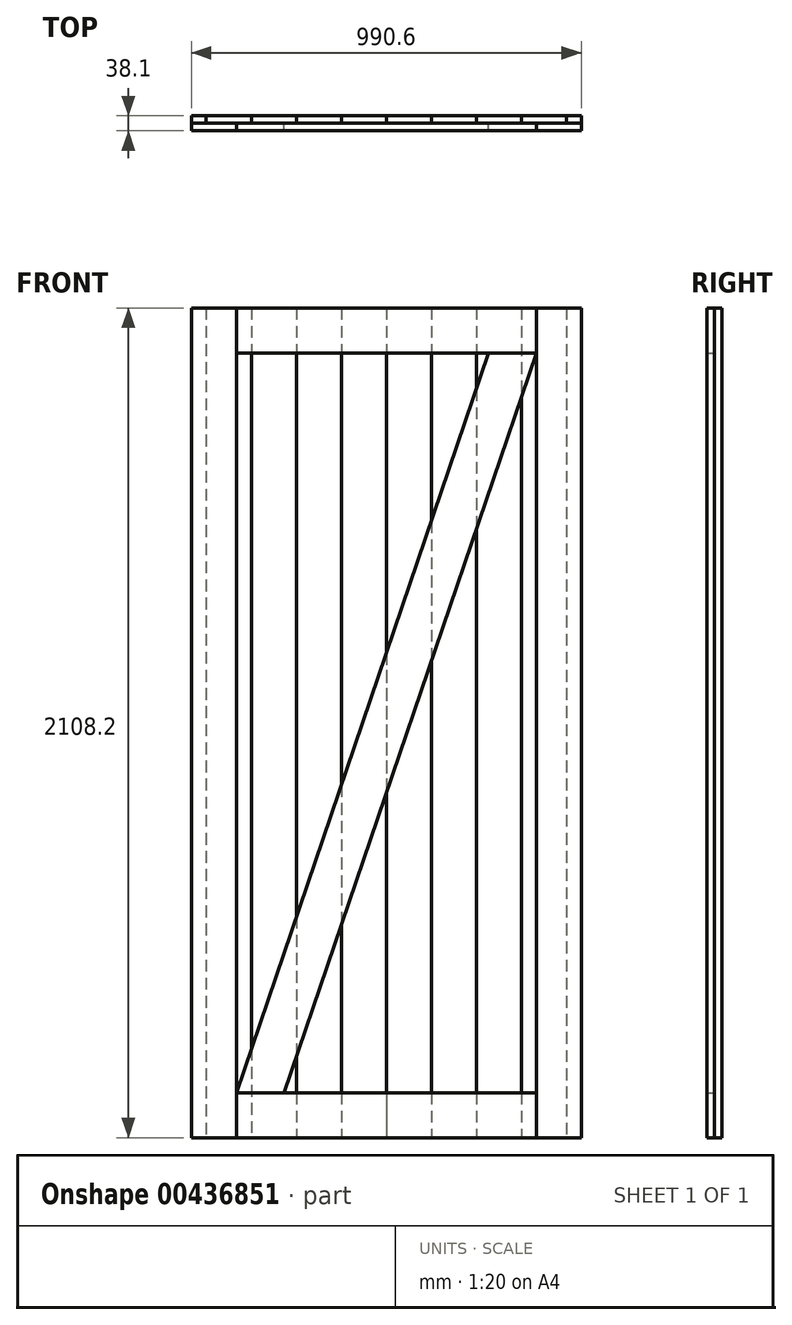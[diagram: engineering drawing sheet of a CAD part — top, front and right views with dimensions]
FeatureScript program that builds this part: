
annotation { "Feature Type Name" : "Feature", "Feature Type Description" : "" }
export const myFeature = defineFeature(function(context is Context, id is Id, definition is map)
    precondition{}
    {
        {
            var Q0;
            Q0=qCreatedBy(makeId("Top.planeOp"),FACE);
            var sketch = newSketch(context, id + "F0", { "sketchPlane" : qUnion([Q0])});
            skLineSegment(sketch, "E0.bottom", {"start": v(0, 0) * mm, "end": v(114.3, 0) * mm});
            skLineSegment(sketch, "E0.top", {"start": v(0, 19.05) * mm, "end": v(114.3, 19.05) * mm});
            skLineSegment(sketch, "E0.left", {"start": v(0, 0) * mm, "end": v(0, 19.05) * mm});
            skLineSegment(sketch, "E0.right", {"start": v(114.3, 0) * mm, "end": v(114.3, 19.05) * mm});
            skSolve(sketch);
        }
        {
            var Q0;
            Q0 = qSketchRegion(id + "F0", true);
            extrude(context, id + "F1", {"entities" : qUnion([Q0]), "depth" : 2108.2 * mm});
        }
        {
            var Q0;
            Q0=makeQuery(id+"F1.opExtrude","SWEPT_BODY",BODY,{"disambiguationData":[OSD([sQuery(id+"F0.wireOp",EDGE,"E0.bottom"),sQuery(id+"F0.wireOp",EDGE,"E0.top"),sQuery(id+"F0.wireOp",EDGE,"E0.left"),sQuery(id+"F0.wireOp",EDGE,"E0.right")])]});
            var Q1;
            Q1=makeQuery(id+"F1.opExtrude","CAP_EDGE",EDGE,{"disambiguationData":[OSD([sQuery(id+"F0.wireOp",EDGE,"E0.bottom")])],"isStart":true});
            transform(context, id + "F2", {"entities" : qUnion([Q0]), "transformType" : TransformType.TRANSLATION_ENTITY, "oppositeDirectionEntity" : false, "transformLine" : qUnion([Q1]), "makeCopy" : true});
        }
        {
            var Q0;
            Q0=makeQuery(id+"F1.opExtrude","SWEPT_BODY",BODY,{"disambiguationData":[OSD([sQuery(id+"F0.wireOp",EDGE,"E0.bottom"),sQuery(id+"F0.wireOp",EDGE,"E0.top"),sQuery(id+"F0.wireOp",EDGE,"E0.left"),sQuery(id+"F0.wireOp",EDGE,"E0.right")])]});
            var Q1;
            Q1=makeQuery(id+"F2.opPattern","COPY",BODY,{"derivedFrom":makeQuery(id+"F1.opExtrude","SWEPT_BODY",BODY,{"disambiguationData":[OSD([sQuery(id+"F0.wireOp",EDGE,"E0.bottom"),sQuery(id+"F0.wireOp",EDGE,"E0.top"),sQuery(id+"F0.wireOp",EDGE,"E0.left"),sQuery(id+"F0.wireOp",EDGE,"E0.right")])]}),"instanceName":"1"});
            var Q2;
            Q2=makeQuery(id+"F1.opExtrude","CAP_FACE",FACE,{"disambiguationData":[OSD([sQuery(id+"F0.wireOp",EDGE,"E0.bottom"),sQuery(id+"F0.wireOp",EDGE,"E0.top"),sQuery(id+"F0.wireOp",EDGE,"E0.left"),sQuery(id+"F0.wireOp",EDGE,"E0.right")])],"isStart":true});
            var Q3;
            Q3=makeQuery(id+"F2.opPattern","COPY",EDGE,{"derivedFrom":makeQuery(id+"F1.opExtrude","CAP_EDGE",EDGE,{"disambiguationData":[OSD([sQuery(id+"F0.wireOp",EDGE,"E0.bottom")])],"isStart":true}),"instanceName":"1"});
            transform(context, id + "F3", {"entities" : qUnion([Q0, Q1]), "transformType" : TransformType.TRANSLATION_DISTANCE, "transformDirection" : qUnion([Q2, Q3]), "distance" : 228.6 * mm, "makeCopy" : true});
        }
        {
            var Q0;
            Q0=makeQuery(id+"F1.opExtrude","SWEPT_BODY",BODY,{"disambiguationData":[OSD([sQuery(id+"F0.wireOp",EDGE,"E0.bottom"),sQuery(id+"F0.wireOp",EDGE,"E0.top"),sQuery(id+"F0.wireOp",EDGE,"E0.left"),sQuery(id+"F0.wireOp",EDGE,"E0.right")])]});
            var Q1;
            Q1=makeQuery(id+"F2.opPattern","COPY",BODY,{"derivedFrom":makeQuery(id+"F1.opExtrude","SWEPT_BODY",BODY,{"disambiguationData":[OSD([sQuery(id+"F0.wireOp",EDGE,"E0.bottom"),sQuery(id+"F0.wireOp",EDGE,"E0.top"),sQuery(id+"F0.wireOp",EDGE,"E0.left"),sQuery(id+"F0.wireOp",EDGE,"E0.right")])]}),"instanceName":"1"});
            var Q2;
            Q2=makeQuery(id+"F3.opPattern","COPY",BODY,{"derivedFrom":makeQuery(id+"F1.opExtrude","SWEPT_BODY",BODY,{"disambiguationData":[OSD([sQuery(id+"F0.wireOp",EDGE,"E0.bottom"),sQuery(id+"F0.wireOp",EDGE,"E0.top"),sQuery(id+"F0.wireOp",EDGE,"E0.left"),sQuery(id+"F0.wireOp",EDGE,"E0.right")])]}),"instanceName":"1"});
            var Q3;
            Q3=makeQuery(id+"F3.opPattern","COPY",BODY,{"derivedFrom":makeQuery(id+"F2.opPattern","COPY",BODY,{"derivedFrom":makeQuery(id+"F1.opExtrude","SWEPT_BODY",BODY,{"disambiguationData":[OSD([sQuery(id+"F0.wireOp",EDGE,"E0.bottom"),sQuery(id+"F0.wireOp",EDGE,"E0.top"),sQuery(id+"F0.wireOp",EDGE,"E0.left"),sQuery(id+"F0.wireOp",EDGE,"E0.right")])]}),"instanceName":"1"}),"instanceName":"1"});
            var Q4;
            Q4=makeQuery(id+"F3.opPattern","COPY",EDGE,{"derivedFrom":makeQuery(id+"F2.opPattern","COPY",EDGE,{"derivedFrom":makeQuery(id+"F1.opExtrude","CAP_EDGE",EDGE,{"disambiguationData":[OSD([sQuery(id+"F0.wireOp",EDGE,"E0.bottom")])],"isStart":true}),"instanceName":"1"}),"instanceName":"1"});
            transform(context, id + "F4", {"entities" : qUnion([Q0, Q1, Q2, Q3]), "transformType" : TransformType.TRANSLATION_DISTANCE, "transformDirection" : qUnion([Q4]), "distance" : 457.2 * mm, "makeCopy" : true});
        }
        {
            var Q0;
            Q0=qCreatedBy(makeId("Top.planeOp"),FACE);
            var sketch = newSketch(context, id + "F5", { "sketchPlane" : qUnion([Q0])});
            skLineSegment(sketch, "E1.bottom", {"start": v(0, 0) * mm, "end": v(-38.1, 0) * mm});
            skLineSegment(sketch, "E1.top", {"start": v(0, 19.05) * mm, "end": v(-38.1, 19.05) * mm});
            skLineSegment(sketch, "E1.left", {"start": v(0, 0) * mm, "end": v(0, 19.05) * mm});
            skLineSegment(sketch, "E1.right", {"start": v(-38.1, 0) * mm, "end": v(-38.1, 19.05) * mm});
            skSolve(sketch);
        }
        {
            var Q0;
            Q0=makeQuery(id+"F5.imprint","IMPRINT",FACE,{"disambiguationData":[TD([[makeQuery(id+"F5.imprint","IMPRINT",EDGE,{"derivedFrom":sQuery(id+"F5.wireOp",EDGE,"E1.bottom")}),-1.0]])]});
            extrude(context, id + "F6", {"entities" : qUnion([Q0]), "depth" : 2108.2 * mm});
        }
        {
            var Q0;
            Q0=makeQuery(id+"F6.opExtrude","SWEPT_BODY",BODY,{"disambiguationData":[OSD([sQuery(id+"F5.wireOp",EDGE,"E1.bottom"),sQuery(id+"F5.wireOp",EDGE,"E1.top"),sQuery(id+"F5.wireOp",EDGE,"E1.left"),sQuery(id+"F5.wireOp",EDGE,"E1.right")])]});
            var Q1;
            Q1=makeQuery(id+"F1.opExtrude","CAP_EDGE",EDGE,{"disambiguationData":[OSD([sQuery(id+"F0.wireOp",EDGE,"E0.top")])],"isStart":false});
            transform(context, id + "F7", {"entities" : qUnion([Q0]), "transformType" : TransformType.TRANSLATION_DISTANCE, "transformDirection" : qUnion([Q1]), "distance" : 952.5 * mm, "makeCopy" : true});
        }
        {
            var Q0;
            Q0=makeQuery(id+"F1.opExtrude","SWEPT_BODY",BODY,{"disambiguationData":[OSD([sQuery(id+"F0.wireOp",EDGE,"E0.bottom"),sQuery(id+"F0.wireOp",EDGE,"E0.top"),sQuery(id+"F0.wireOp",EDGE,"E0.left"),sQuery(id+"F0.wireOp",EDGE,"E0.right")])]});
            transform(context, id + "F8", {"entities" : qUnion([Q0]), "transformType" : TransformType.TRANSLATION_3D, "dx" : -38.1 * mm, "dy" : -19.05 * mm, "dz" : 0 * mm, "makeCopy" : true});
        }
        {
            var Q0;
            Q0=makeQuery(id+"F8.opPattern","COPY",BODY,{"derivedFrom":makeQuery(id+"F1.opExtrude","SWEPT_BODY",BODY,{"disambiguationData":[OSD([sQuery(id+"F0.wireOp",EDGE,"E0.bottom"),sQuery(id+"F0.wireOp",EDGE,"E0.top"),sQuery(id+"F0.wireOp",EDGE,"E0.left"),sQuery(id+"F0.wireOp",EDGE,"E0.right")])]}),"instanceName":"1"});
            transform(context, id + "F9", {"entities" : qUnion([Q0]), "transformType" : TransformType.TRANSLATION_3D, "dx" : 876.3 * mm, "dy" : 0 * mm, "dz" : 0 * mm, "makeCopy" : true});
        }
        {
            var Q0;
            Q0=makeQuery(id+"F2.opPattern","COPY",FACE,{"derivedFrom":makeQuery(id+"F1.opExtrude","SWEPT_FACE",FACE,{"disambiguationData":[OSD([sQuery(id+"F0.wireOp",EDGE,"E0.bottom")])]}),"instanceName":"1"});
            var sketch = newSketch(context, id + "F10", { "sketchPlane" : qUnion([Q0])});
            skPoint(sketch, "E2.firstSnap0", {"position": v(171.45, 2108.2) * mm});
            skLineSegment(sketch, "E2.bottom", {"start": v(76.2, 2108.2) * mm, "end": v(838.2, 2108.2) * mm});
            skLineSegment(sketch, "E2.top", {"start": v(76.2, 1993.9) * mm, "end": v(838.2, 1993.9) * mm});
            skLineSegment(sketch, "E2.left", {"start": v(76.2, 2108.2) * mm, "end": v(76.2, 1993.9) * mm});
            skLineSegment(sketch, "E2.right", {"start": v(838.2, 2108.2) * mm, "end": v(838.2, 1993.9) * mm});
            skSolve(sketch);
        }
        {
            var Q0;
            Q0 = qSketchRegion(id + "F10", true);
            extrude(context, id + "F11", {"entities" : qUnion([Q0]), "depth" : 19.05 * mm});
        }
        {
            var Q0;
            Q0=makeQuery(id+"F11.opExtrude","SWEPT_BODY",BODY,{"disambiguationData":[OSD([sQuery(id+"F10.wireOp",EDGE,"E2.bottom"),sQuery(id+"F10.wireOp",EDGE,"E2.top"),sQuery(id+"F10.wireOp",EDGE,"E2.left"),sQuery(id+"F10.wireOp",EDGE,"E2.right")])]});
            transform(context, id + "F12", {"entities" : qUnion([Q0]), "transformType" : TransformType.TRANSLATION_3D, "dx" : 0 * mm, "dy" : 0 * mm, "dz" : -1993.9 * mm, "makeCopy" : true});
        }
        {
            var Q0;
            Q0=makeQuery(id+"F2.opPattern","COPY",FACE,{"derivedFrom":makeQuery(id+"F1.opExtrude","SWEPT_FACE",FACE,{"disambiguationData":[OSD([sQuery(id+"F0.wireOp",EDGE,"E0.bottom")])]}),"instanceName":"1"});
            var sketch = newSketch(context, id + "F13", { "sketchPlane" : qUnion([Q0])});
            skLineSegment(sketch, "E3", {"start": v(730.02, 2030.8) * mm, "end": v(76.2, 114.3) * mm, "construction": true});
            skLineSegment(sketch, "E4", {"start": v(76.2, 114.3) * mm, "end": v(184.38, 77.4) * mm, "construction": true});
            skLineSegment(sketch, "E5", {"start": v(184.38, 77.4) * mm, "end": v(838.2, 1993.9) * mm, "construction": true});
            skLineSegment(sketch, "E6", {"start": v(838.2, 1993.9) * mm, "end": v(730.02, 2030.8) * mm, "construction": true});
            skLineSegment(sketch, "E7", {"start": v(76.2, 114.3) * mm, "end": v(196.97, 114.3) * mm});
            skLineSegment(sketch, "E8", {"start": v(838.2, 1993.9) * mm, "end": v(717.43, 1993.9) * mm});
            skLineSegment(sketch, "E9", {"start": v(838.2, 1993.9) * mm, "end": v(196.97, 114.3) * mm});
            skLineSegment(sketch, "E10", {"start": v(76.2, 114.3) * mm, "end": v(717.43, 1993.9) * mm});
            skSolve(sketch);
        }
        {
            var Q0;
            Q0 = qSketchRegion(id + "F13", true);
            extrude(context, id + "F14", {"entities" : qUnion([Q0]), "depth" : 19.05 * mm});
        }
    });
